# Revit family: Gira_018500
name_source: partatom
category: Allgemeines Modell
revit_build: Autodesk Revit 2017 (Build: 20160225_1515(x64)
units: mm (PartAtom-declared; Revit-internal decimal feet)

## family parameters
Basisbauteil = Fläche
Beim Laden mit Abzugskörper schneiden = Nein
Bemaßung runder Anschluss = Durchmesser verwenden
Gemeinsam genutzt = Nein
Kann Basisbauteil für Bewehrung sein = Nein
Raumberechnungspunkt = Nein
Teiletyp = Normal

## types (1)
- Gira_018500
    Assembly arrangement = Basic element
    BIM = https://media.stage.bim.site
    Beschreibung = Ins.b.cpl.btn 2g 2-pt KNX,Insert for KNX bus coupler button, 2-gang with 2-point operation,,,The bus coupler button is the interface between the KNX system and the user.,,Features:,- The rockers, 2-gang of the flush-mounted design lines can be inserted on the bus coupler button, 2-gang with two-point operation (upright rocker).,- The bus coupler button, 2-gang with two-point operation can be used to realise the functions switching (pressing), blind, dimming with stop telegram and dimming with cyclical transmission.,,Notes :,- Suitable for claw mounting.,- Please use System 55 adapter frame and cover for Gira TX_44 design line, IP20.,- Integration in the Gira F100 design line is not possible.,- Integration in Gira F100 not possible.
    Bus system KNX = Ja
    Bus system KNX radio = Nein
    Bus system LON = Nein
    Bus system Powernet = Nein
    Bus system radio frequent = Nein
    Colour = Other
    Data sheet = https://katalog.gira.de
    Frequency [Hz] = [50:50]
    GTIN = 4010337185000
    HAN = 018500
    Halogen free = Nein
    Hersteller = Gira
    Integrated timer = Nein
    Material = Other
    Material quality = Other
    Max. switching power [Voltampere] = 1000
    Mounting method = Flush mounted (plaster)
    Nominal voltage [Volt] = 230
    Other bus systems = None
    Productwebsite = http://katalog.gira.de
    Radio frequent bidirectional = Nein
    Random generator = Nein
    Substation input = Nein
    Suitable for degree of protection (IP) = IP20
    Suitable for rain sensor = Nein
    Suitable for wind sensor = Nein
    Surface finishing = Not applicable
    Surface protection = Other
    Switch-off protection = Nein
    Transparent = Nein
    Type of fastening = Mounting with claw and screw
    Typname = Bus coup.btn 2-g 2-point KNX insert
    URL = https://www.gira.de
    Vorgabe-Ansicht = 1219 mm
    With Astro program = Nein
    With brightness sensor connection = Nein
    With glass breaking detector connection = Nein
    With memory function = Nein

## geometry (parser evidence)
native form markers: Sweep x2
no freeform markers — native parametric forms only
